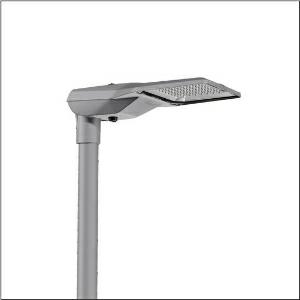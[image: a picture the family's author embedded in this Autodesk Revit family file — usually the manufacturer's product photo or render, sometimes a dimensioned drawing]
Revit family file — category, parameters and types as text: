
# Revit family: streetlight_sl_21_midi___stw1_0a_5xe3e43t08lb_2539
name_source: partatom
category: Lighting Fixtures
units: mm (PartAtom-declared; Revit-internal decimal feet)

## family parameters
Cut with Voids When Loaded = No
Host = Face
Light Source = No
Part Type = Normal
Room Calculation Point = No
Round Connector Dimension = Use Diameter
Shared = No

## types (1)
- --- (1 x LED, 14950 lm, 99.6 W, 4000K)
    Apparent Load = 100 VA
    CIE Flux Codes = 38 75 98 100 100
    Color Rendering = 70
    Color Temperature = 4000K
    Default Elevation = 1800 mm
    Description = Streetlight SL 21 midi, mast luminaire, primary light control with lens, of PMMA, primary optical cover: cover, of toughened safety glass, transparent, light distribution: STW1.0a, light emission: direct distribution, primary light characteristic: asymmetric, installation type: side-entry, post-top, LED, High Power LED, rated luminous flux: 14.950lm, luminous efficacy: 150lm/W, light colour: 740, colour temperature: 4000K, control gear: D4i, control: overheat protection, constant luminous flux control, time-dependent luminous flux control, flexible luminous flux parameterisation, pre-setting: logarithmic dimming characteristic, mains connection: 230..240V, AC, 50/60Hz, start of lifetime: 100W, end of service life: 102W, reduction: 46W, luminaire housing, of diecast aluminium, powder-coated, SITECO metallic grey (DB 702S), corrosivity category C5 high according to DIN EN ISO 12944, please order mast flange separately, inclination adjustable: 0°, 5°, 10°, 15°, sealing non-destructively replaceable, multi-level sealing system, length: 644mm, width: 335mm, height: 110mm, mast flange for spigot size: 42mm (side-entry): 5XC10008XM4, 60/48mm (side-entry/post-top): 5XC10108XM2, 76/60mm (side-entry/post-top): 5XC10108XM1, mounting height: 4..8m, Smart Interface below and above, protection rating (complete): IP66, insulation class (complete): insulation class II (safety insulation), certification: CE, ENEC, ENEC+, VDE, impact resistance: IK10, permissible operating ambient temperature for outdoor applications: -40..+50°C, standard-compliant lighting for roads and squares, packaging unit: 1 piece

Light Distribution: STW1.0a
    Height = 111 mm
    Lamp = 1 x LED
    Lamp Light Flux = 14950 lm
    Lamp Power = 99.6 W
    Lamp count = 1
    Length = 644 mm
    Luminous efficacy = 150 lm/W
    Manufacturer = Siteco
    ModVariant = No
    Model = 5XE3E43T08LB
    Number of Poles = 1
    OnlyDefault = Yes
    Power Factor = 1
    Product Name = Streetlight SL 21 midi | STW1.0a
    Product group = mast luminaire | pylon top
    ProductGroupID = 6100
    Protection Class = Protection class II
    Protection Degree = IP 66
    RLX_Detail_Level = 1
    RLX_Emergency_Light_Flux = 0 lm
    RLX_Emergency_Type = 0
    RLX_Emergency_Type_DB = No
    RlxData = <blob elided: 26901 chars, md5=78125ab5>
    Socket = socket
    Standby Power = 0 W
    System Light Flux = 14950 lm
    System Power = 100 W
    Type Comments = factory setting: luminous flux: 100 % | dim-lin: 254 | 1020 mA
    Type Image = l_1004304.jpg
    URL = http://relux.com
    VarID = @adj_031539
    Voltage = 0 V
    Weight = 0.00 kg
    Width = 336 mm

## geometry (parser evidence)
native form markers: Blend x4, Sweep x10
no freeform markers — native parametric forms only
